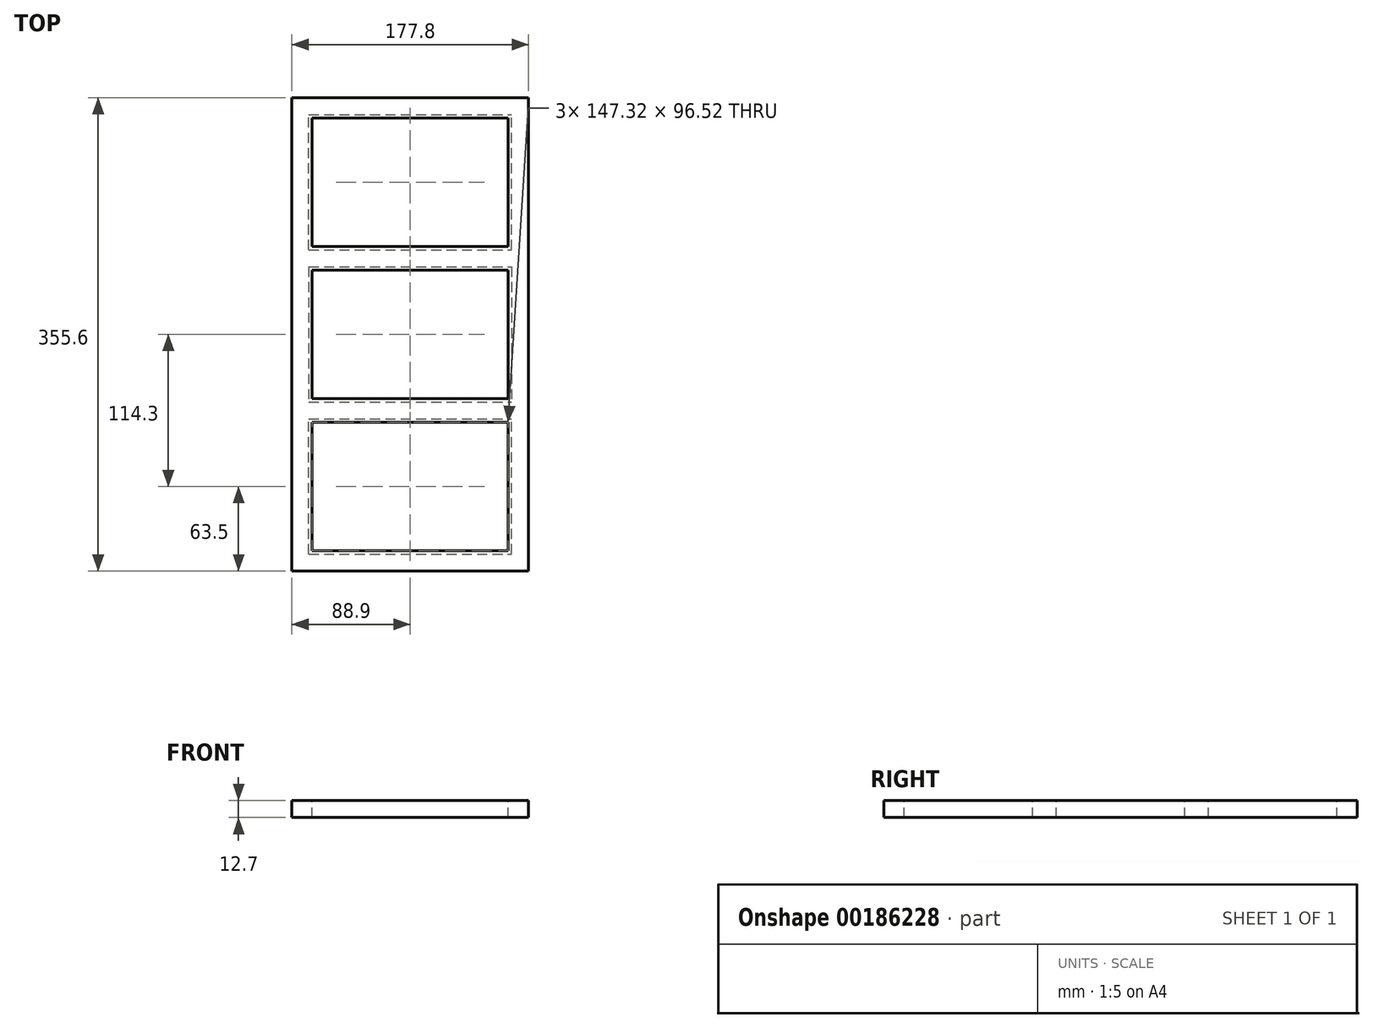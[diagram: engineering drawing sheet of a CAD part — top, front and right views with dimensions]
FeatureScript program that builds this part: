
annotation { "Feature Type Name" : "Feature", "Feature Type Description" : "" }
export const myFeature = defineFeature(function(context is Context, id is Id, definition is map)
    precondition{}
    {
        {
            var Q0;
            Q0=qCreatedBy(makeId("Top.planeOp"),FACE);
            var sketch = newSketch(context, id + "F0", { "sketchPlane" : qUnion([Q0])});
            skLineSegment(sketch, "E0.bottom", {"start": v(88.9, -177.8) * mm, "end": v(-88.9, -177.8) * mm});
            skLineSegment(sketch, "E0.top", {"start": v(88.9, 177.8) * mm, "end": v(-88.9, 177.8) * mm});
            skLineSegment(sketch, "E0.left", {"start": v(88.9, -177.8) * mm, "end": v(88.9, 177.8) * mm});
            skLineSegment(sketch, "E0.right", {"start": v(-88.9, -177.8) * mm, "end": v(-88.9, 177.8) * mm});
            skPoint(sketch, "E0.middle", {"position": v(0, 0) * mm});
            skLineSegment(sketch, "E1", {"start": v(-88.9, 118.53) * mm, "end": v(88.9, 118.53) * mm, "construction": true});
            skLineSegment(sketch, "E2", {"start": v(-88.9, -118.53) * mm, "end": v(88.9, -118.53) * mm, "construction": true});
            skSolve(sketch);
        }
        {
            var Q0;
            Q0=makeQuery(id+"F0.imprint","IMPRINT",FACE,{"disambiguationData":[TD([[makeQuery(id+"F0.imprint","IMPRINT",EDGE,{"derivedFrom":sQuery(id+"F0.wireOp",EDGE,"E0.bottom")}),-1.0]])]});
            var sketch = newSketch(context, id + "F1", { "sketchPlane" : qUnion([Q0])});
            skLineSegment(sketch, "E3.bottom", {"start": v(-73.66, 162.56) * mm, "end": v(73.66, 162.56) * mm});
            skLineSegment(sketch, "E3.top", {"start": v(-73.66, 66.04) * mm, "end": v(73.66, 66.04) * mm});
            skLineSegment(sketch, "E3.left", {"start": v(-73.66, 162.56) * mm, "end": v(-73.66, 66.04) * mm});
            skLineSegment(sketch, "E3.right", {"start": v(73.66, 162.56) * mm, "end": v(73.66, 66.04) * mm});
            skPoint(sketch, "E3.middle", {"position": v(0, 114.3) * mm});
            skLineSegment(sketch, "E4.bottom", {"start": v(-73.66, 48.26) * mm, "end": v(73.66, 48.26) * mm});
            skLineSegment(sketch, "E4.top", {"start": v(-73.66, -48.26) * mm, "end": v(73.66, -48.26) * mm});
            skLineSegment(sketch, "E4.left", {"start": v(-73.66, 48.26) * mm, "end": v(-73.66, -48.26) * mm});
            skLineSegment(sketch, "E4.right", {"start": v(73.66, 48.26) * mm, "end": v(73.66, -48.26) * mm});
            skPoint(sketch, "E4.middle", {"position": v(0, 0) * mm});
            skLineSegment(sketch, "E5.bottom", {"start": v(-73.66, -162.56) * mm, "end": v(73.66, -162.56) * mm});
            skLineSegment(sketch, "E5.top", {"start": v(-73.66, -66.04) * mm, "end": v(73.66, -66.04) * mm});
            skLineSegment(sketch, "E5.left", {"start": v(-73.66, -162.56) * mm, "end": v(-73.66, -66.04) * mm});
            skLineSegment(sketch, "E5.right", {"start": v(73.66, -162.56) * mm, "end": v(73.66, -66.04) * mm});
            skPoint(sketch, "E5.middle", {"position": v(0, -114.3) * mm});
            skSolve(sketch);
        }
        {
            var Q0;
            Q0=makeQuery(id+"F0.imprint","IMPRINT",FACE,{"disambiguationData":[TD([[makeQuery(id+"F0.imprint","IMPRINT",EDGE,{"derivedFrom":sQuery(id+"F0.wireOp",EDGE,"E0.bottom")}),-1.0]])]});
            extrude(context, id + "F2", {"entities" : qUnion([Q0]), "oppositeDirection" : true, "depth" : 12.7 * mm});
        }
        {
            var Q0;
            Q0=makeQuery(id+"F2.opExtrude","SWEPT_FACE",FACE,{"disambiguationData":[OSD([sQuery(id+"F0.wireOp",EDGE,"E0.bottom")])]});
            var sketch = newSketch(context, id + "F3", { "sketchPlane" : qUnion([Q0])});
            skCircle(sketch, "E6", {"center": v(-88.9, 0) * mm, "radius": 3.18 * mm});
            skCircle(sketch, "E7", {"center": v(88.9, 0) * mm, "radius": 3.18 * mm});
            skSolve(sketch);
        }
        {
            var Q0;
            Q0=makeQuery(id+"F1.imprint","IMPRINT",FACE,{"disambiguationData":[TD([[makeQuery(id+"F1.imprint","IMPRINT",EDGE,{"derivedFrom":sQuery(id+"F1.wireOp",EDGE,"E5.bottom")}),1.0]])]});
            var Q1;
            Q1=makeQuery(id+"F1.imprint","IMPRINT",FACE,{"disambiguationData":[TD([[makeQuery(id+"F1.imprint","IMPRINT",EDGE,{"derivedFrom":sQuery(id+"F1.wireOp",EDGE,"E4.bottom")}),-1.0]])]});
            var Q2;
            Q2=makeQuery(id+"F1.imprint","IMPRINT",FACE,{"disambiguationData":[TD([[makeQuery(id+"F1.imprint","IMPRINT",EDGE,{"derivedFrom":sQuery(id+"F1.wireOp",EDGE,"E3.bottom")}),-1.0]])]});
            extrude(context, id + "F4", {"entities" : qUnion([Q0, Q1, Q2]), "operationType" : NewBodyOperationType.REMOVE, "endBound" : BoundingType.THROUGH_ALL, "oppositeDirection" : true, "depth" : 25.4 * mm});
        }
        {
            var Q0;
            Q0=makeQuery(id+"F4.boolean.opBoolean","COPY",FACE,{"derivedFrom":makeQuery(id+"F4.opExtrude","SWEPT_FACE",FACE,{"disambiguationData":[OSD([sQuery(id+"F1.wireOp",EDGE,"E5.top")])]})});
            var sketch = newSketch(context, id + "F5", { "sketchPlane" : qUnion([Q0])});
            skCircle(sketch, "E8", {"center": v(-73.66, 0) * mm, "radius": 3.18 * mm});
            skSolve(sketch);
        }
        {
            var Q0;
            Q0=makeQuery(id+"F4.boolean.opBoolean","COPY",FACE,{"derivedFrom":makeQuery(id+"F4.opExtrude","SWEPT_FACE",FACE,{"disambiguationData":[OSD([sQuery(id+"F1.wireOp",EDGE,"E4.bottom")])]})});
            var sketch = newSketch(context, id + "F6", { "sketchPlane" : qUnion([Q0])});
            skCircle(sketch, "E9", {"center": v(-73.66, 0) * mm, "radius": 3.18 * mm});
            skSolve(sketch);
        }
        {
            var Q0;
            Q0=makeQuery(id+"F4.boolean.opBoolean","COPY",FACE,{"derivedFrom":makeQuery(id+"F4.opExtrude","SWEPT_FACE",FACE,{"disambiguationData":[OSD([sQuery(id+"F1.wireOp",EDGE,"E3.bottom")])]})});
            var sketch = newSketch(context, id + "F7", { "sketchPlane" : qUnion([Q0])});
            skCircle(sketch, "E10", {"center": v(-73.66, 0) * mm, "radius": 3.18 * mm});
            skSolve(sketch);
        }
        {
            var Q0;
            Q0=makeQuery(id+"F2.opExtrude","CAP_FACE",FACE,{"disambiguationData":[OSD([sQuery(id+"F0.wireOp",EDGE,"E0.bottom"),sQuery(id+"F0.wireOp",EDGE,"E0.top"),sQuery(id+"F0.wireOp",EDGE,"E0.left"),sQuery(id+"F0.wireOp",EDGE,"E0.right")])],"isStart":false});
            var sketch = newSketch(context, id + "F8", { "sketchPlane" : qUnion([Q0])});
            skLineSegment(sketch, "E11.bottom", {"start": v(-76.2, -63.5) * mm, "end": v(76.2, -63.5) * mm});
            skLineSegment(sketch, "E11.top", {"start": v(-76.2, -165.1) * mm, "end": v(76.2, -165.1) * mm});
            skLineSegment(sketch, "E11.left", {"start": v(-76.2, -63.5) * mm, "end": v(-76.2, -165.1) * mm});
            skLineSegment(sketch, "E11.right", {"start": v(76.2, -63.5) * mm, "end": v(76.2, -165.1) * mm});
            skPoint(sketch, "E11.middle", {"position": v(0, -114.3) * mm});
            skPoint(sketch, "E11.middle.positionSnap0", {"position": v(73.66, -114.3) * mm});
            skPoint(sketch, "E11.middle.positionSnap1", {"position": v(0, -162.56) * mm});
            skPoint(sketch, "E11.centerSnap0", {"position": v(73.66, -114.3) * mm});
            skPoint(sketch, "E11.centerSnap1", {"position": v(0, -162.56) * mm});
            skLineSegment(sketch, "E12.bottom", {"start": v(-76.2, -50.8) * mm, "end": v(76.2, -50.8) * mm});
            skLineSegment(sketch, "E12.top", {"start": v(-76.2, 50.8) * mm, "end": v(76.2, 50.8) * mm});
            skLineSegment(sketch, "E12.left", {"start": v(-76.2, -50.8) * mm, "end": v(-76.2, 50.8) * mm});
            skLineSegment(sketch, "E12.right", {"start": v(76.2, -50.8) * mm, "end": v(76.2, 50.8) * mm});
            skPoint(sketch, "E12.middle", {"position": v(0, 0) * mm});
            skLineSegment(sketch, "E13.bottom", {"start": v(-76.2, 165.1) * mm, "end": v(76.2, 165.1) * mm});
            skLineSegment(sketch, "E13.top", {"start": v(-76.2, 63.5) * mm, "end": v(76.2, 63.5) * mm});
            skLineSegment(sketch, "E13.left", {"start": v(-76.2, 165.1) * mm, "end": v(-76.2, 63.5) * mm});
            skLineSegment(sketch, "E13.right", {"start": v(76.2, 165.1) * mm, "end": v(76.2, 63.5) * mm});
            skPoint(sketch, "E13.middle", {"position": v(0, 114.3) * mm});
            skPoint(sketch, "E13.middle.positionSnap0", {"position": v(73.66, 114.3) * mm});
            skPoint(sketch, "E13.centerSnap0", {"position": v(73.66, 114.3) * mm});
            skSolve(sketch);
        }
        {
            var Q0;
            Q0 = qSketchRegion(id + "F8", true);
            extrude(context, id + "F9", {"entities" : qUnion([Q0]), "operationType" : NewBodyOperationType.REMOVE, "oppositeDirection" : true, "depth" : 3 / 203.2 * mm});
        }
    });
